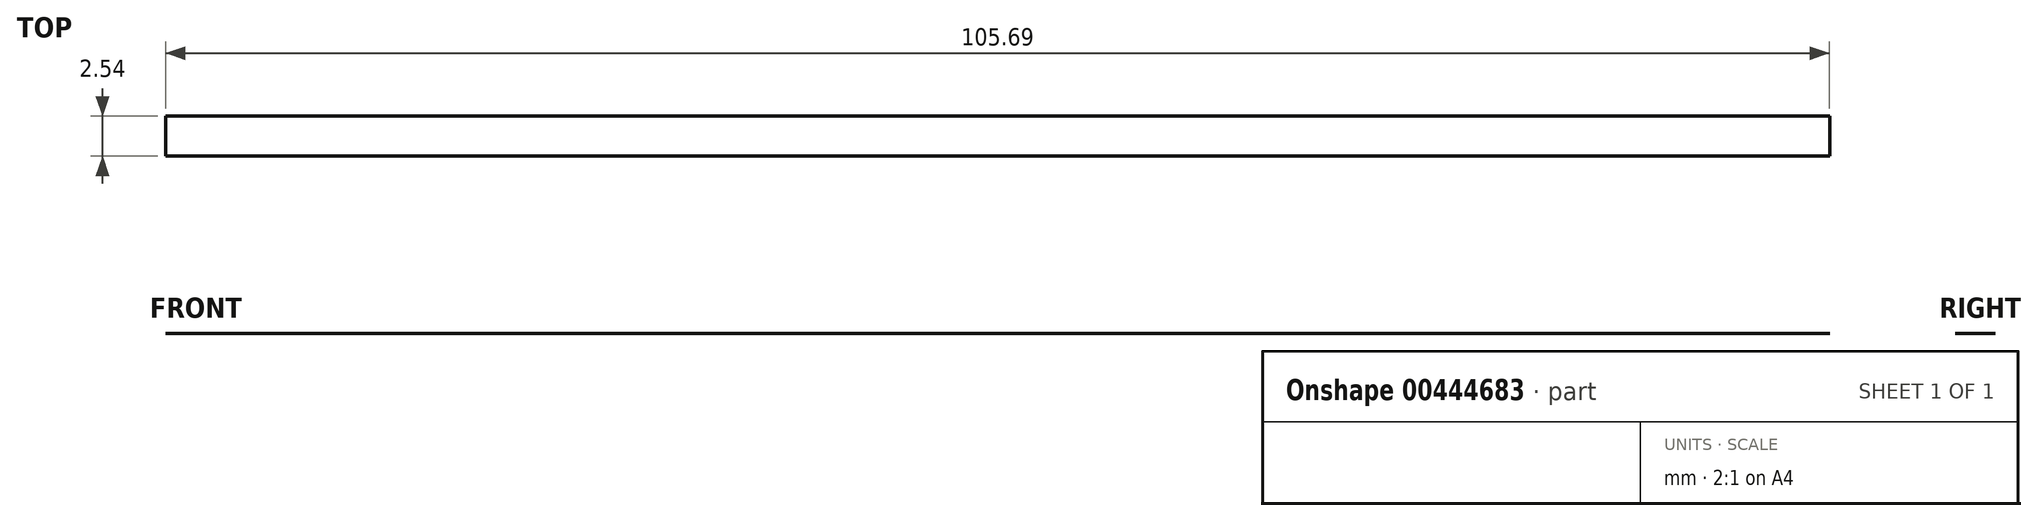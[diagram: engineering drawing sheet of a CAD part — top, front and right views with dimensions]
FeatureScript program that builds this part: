
annotation { "Feature Type Name" : "Feature", "Feature Type Description" : "" }
export const myFeature = defineFeature(function(context is Context, id is Id, definition is map)
    precondition{}
    {
        {
            var Q0;
            Q0=qCreatedBy(makeId("Front.planeOp"),FACE);
            var sketch = newSketch(context, id + "F0", { "sketchPlane" : qUnion([Q0])});
            skLineSegment(sketch, "E0", {"start": v(-48.15, 0) * mm, "end": v(57.54, 0) * mm});
            skSolve(sketch);
        }
        {
            var Q0;
            Q0=sQuery(id+"F0.wireOp",EDGE,"E0");
            extrude(context, id + "F1", {"bodyType" : ToolBodyType.SURFACE, "surfaceEntities" : qUnion([Q0]), "depth" : 2.54 * mm});
        }
    });
